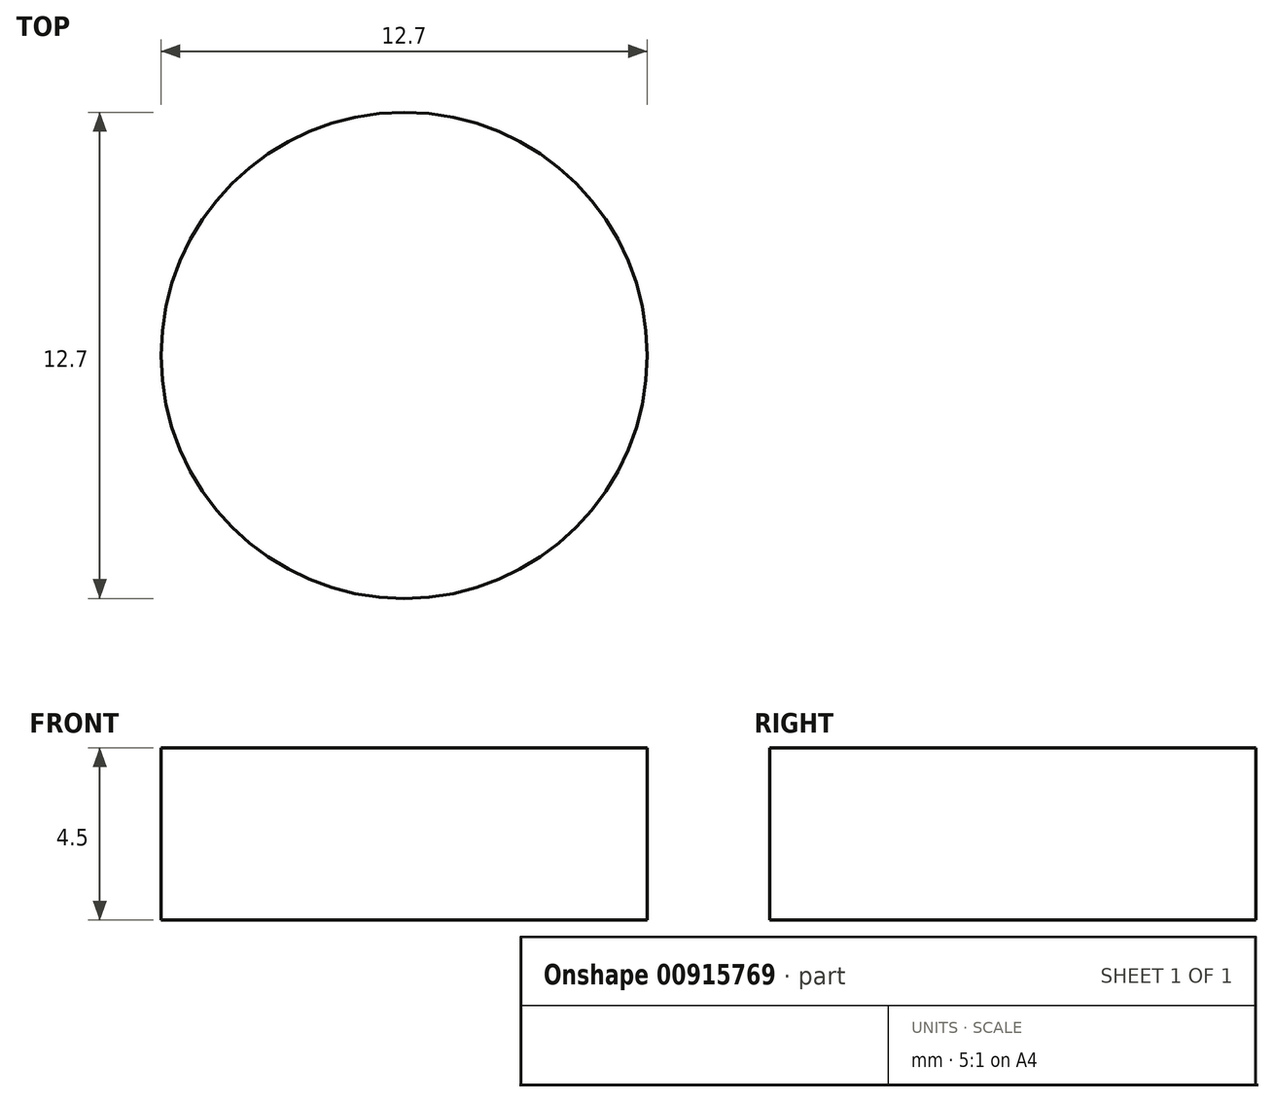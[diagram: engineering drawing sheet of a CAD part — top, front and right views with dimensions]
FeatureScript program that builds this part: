
annotation { "Feature Type Name" : "Feature", "Feature Type Description" : "" }
export const myFeature = defineFeature(function(context is Context, id is Id, definition is map)
    precondition{}
    {
        {
            var Q0;
            Q0=qCreatedBy(makeId("Top.planeOp"),FACE);
            var sketch = newSketch(context, id + "F0", { "sketchPlane" : qUnion([Q0])});
            skCircle(sketch, "E0", {"center": v(0, 0) * mm, "radius": 6.35 * mm});
            skSolve(sketch);
        }
        {
            var Q0;
            Q0=makeQuery(id+"F0.imprint","IMPRINT",FACE,{"disambiguationData":[TD([[makeQuery(id+"F0.imprint","IMPRINT",EDGE,{"derivedFrom":sQuery(id+"F0.wireOp",EDGE,"E0")}),1.0]])]});
            extrude(context, id + "F1", {"entities" : qUnion([Q0]), "depth" : 4.5 * mm, "offsetDistance" : 25 * mm});
        }
    });
